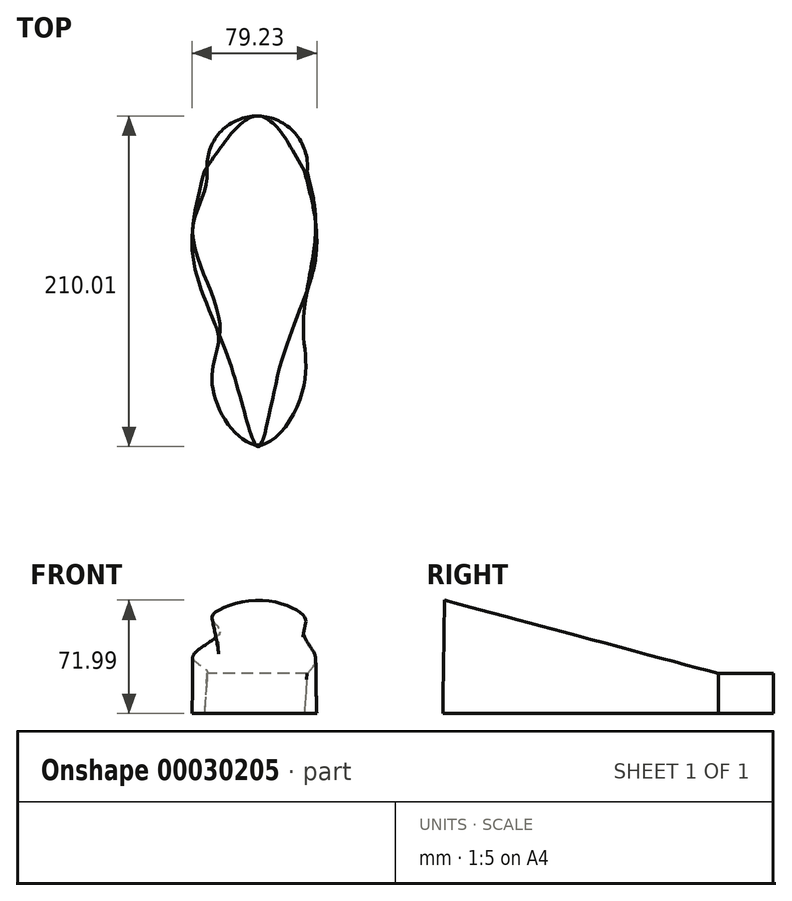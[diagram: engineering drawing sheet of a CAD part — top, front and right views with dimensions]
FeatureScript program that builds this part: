
annotation { "Feature Type Name" : "Feature", "Feature Type Description" : "" }
export const myFeature = defineFeature(function(context is Context, id is Id, definition is map)
    precondition{}
    {
        {
            var Q0;
            Q0=qCreatedBy(makeId("Top.planeOp"),FACE);
            cPlane(context, id + "F0", {"entities" : qUnion([Q0]), "cplaneType" : CPlaneType.OFFSET, "offset" : 25.4 * mm, "width" : 152.4 * mm, "height" : 152.4 * mm});
        }
        {
            var Q0;
            Q0=qCreatedBy(id+"F0.planeOp",FACE);
            var sketch = newSketch(context, id + "F1", { "sketchPlane" : qUnion([Q0])});
            skLineSegment(sketch, "E0.bottom", {"start": v(-25.4, 304.8) * mm, "end": v(31.75, 304.8) * mm});
            skLineSegment(sketch, "E0.top", {"start": v(-25.4, 273.05) * mm, "end": v(31.75, 273.05) * mm});
            skLineSegment(sketch, "E0.left", {"start": v(-25.4, 304.8) * mm, "end": v(-25.4, 273.05) * mm});
            skLineSegment(sketch, "E0.right", {"start": v(31.75, 304.8) * mm, "end": v(31.75, 273.05) * mm});
            skSolve(sketch);
        }
        {
            var Q0;
            Q0=sQuery(id+"F1.wireOp",EDGE,"E0.top");
            cPlane(context, id + "F2", {"entities" : qUnion([Q0]), "cplaneType" : CPlaneType.LINE_ANGLE, "offset" : 152.4 * mm, "angle" : 75 * degree, "width" : 152.4 * mm, "height" : 152.4 * mm});
        }
        {
            var Q0;
            Q0=sQuery(id+"F1.wireOp",EDGE,"E0.top");
            cPlane(context, id + "F3", {"entities" : qUnion([Q0]), "cplaneType" : CPlaneType.LINE_ANGLE, "offset" : 152.4 * mm, "angle" : 0 * degree, "width" : 152.4 * mm, "height" : 152.4 * mm});
        }
        {
            var Q0;
            Q0=qCreatedBy(makeId("Top.planeOp"),FACE);
            var sketch = newSketch(context, id + "F4", { "sketchPlane" : qUnion([Q0])});
            skLineSegment(sketch, "E1", {"start": v(0, 308.05) * mm, "end": v(0, 98.05) * mm, "construction": true});
            skLineSegment(sketch, "E2", {"start": v(-41.54, 218.53) * mm, "end": v(36.46, 218.53) * mm, "construction": true});
            skLineSegment(sketch, "E3", {"start": v(-17.78, 150.56) * mm, "end": v(14.22, 150.56) * mm, "construction": true});
            skLineSegment(sketch, "E4", {"start": v(29.2, 273.05) * mm, "end": v(-34.3, 273.05) * mm, "construction": true});
            skFitSpline(sketch, "E5", {"points": [v(29.2, 273.05) * mm, v(0, 308.05) * mm, v(-34.3, 273.05) * mm], "startDerivative": vector(-57.55, 105.67) * mm, "endDerivative": vector(-69.38, -104.4) * mm});
            skFitSpline(sketch, "E6", {"points": [v(29.2, 273.05) * mm, v(36.46, 218.53) * mm, v(14.22, 150.56) * mm, v(0, 98.05) * mm, v(-17.78, 150.56) * mm, v(-41.54, 218.53) * mm, v(-34.3, 273.05) * mm], "startDerivative": vector(94.08, -343.52) * mm, "endDerivative": vector(86.53, 342.8) * mm});
            skSolve(sketch);
        }
        {
            var Q0;
            Q0=qCreatedBy(id+"F0.planeOp",FACE);
            var sketch = newSketch(context, id + "F5", { "sketchPlane" : qUnion([Q0])});
            skLineSegment(sketch, "E7", {"start": v(0, 308.05) * mm, "end": v(0, 93.05) * mm, "construction": true});
            skLineSegment(sketch, "E8", {"start": v(31.01, 273.05) * mm, "end": v(-32.49, 273.05) * mm, "construction": true});
            skArc(sketch, "E9", {"start": v(31.01, 273.05) * mm, "mid": v(-0.74, 308.06) * mm, "end": v(-32.49, 273.05) * mm});
            skSolve(sketch);
        }
        {
            var Q0;
            Q0=qCreatedBy(id+"F2.planeOp",FACE);
            var sketch = newSketch(context, id + "F6", { "sketchPlane" : qUnion([Q0])});
            skLineSegment(sketch, "E10", {"start": v(0, 292.17) * mm, "end": v(0, 77.17) * mm, "construction": true});
            skLineSegment(sketch, "E11", {"start": v(-41.68, 217.17) * mm, "end": v(36.32, 217.17) * mm, "construction": true});
            skLineSegment(sketch, "E12", {"start": v(-24.46, 156.94) * mm, "end": v(28.54, 156.94) * mm, "construction": true});
            skLineSegment(sketch, "E13", {"start": v(31.01, 257.17) * mm, "end": v(-32.49, 257.17) * mm, "construction": true});
            skLineSegment(sketch, "E14", {"start": v(28.8, 115.45) * mm, "end": v(-29.2, 115.45) * mm, "construction": true});
            skArc(sketch, "E15", {"start": v(31.01, 257.17) * mm, "mid": v(-0.74, 292.18) * mm, "end": v(-32.49, 257.17) * mm, "construction": true});
            skFitSpline(sketch, "E16", {"points": [v(31.01, 257.17) * mm, v(36.32, 217.17) * mm, v(28.54, 156.94) * mm, v(28.8, 115.45) * mm, v(0, 77.17) * mm, v(-29.2, 115.45) * mm, v(-24.46, 156.94) * mm, v(-41.68, 217.17) * mm, v(-32.49, 257.17) * mm], "startDerivative": vector(78.8, -321.4) * mm, "endDerivative": vector(-34.15, 348.95) * mm});
            skSolve(sketch);
        }
        {
            var Q0;
            Q0=sQuery(id+"F5.wireOp",EDGE,"E9");
            var Q1;
            Q1=sQuery(id+"F4.wireOp",EDGE,"E5");
            loft(context, id + "F7", {"bodyType" : ToolBodyType.SURFACE, "wireProfilesArray" : [{ "wireProfileEntities" : qUnion([Q0]) }, { "wireProfileEntities" : qUnion([Q1]) }]});
        }
        {
            var Q0;
            Q0=sQuery(id+"F6.wireOp",EDGE,"E16");
            var Q1;
            Q1=sQuery(id+"F4.wireOp",EDGE,"E6");
            loft(context, id + "F8", {"bodyType" : ToolBodyType.SURFACE, "wireProfilesArray" : [{ "wireProfileEntities" : qUnion([Q0]) }, { "wireProfileEntities" : qUnion([Q1]) }]});
        }
    });
